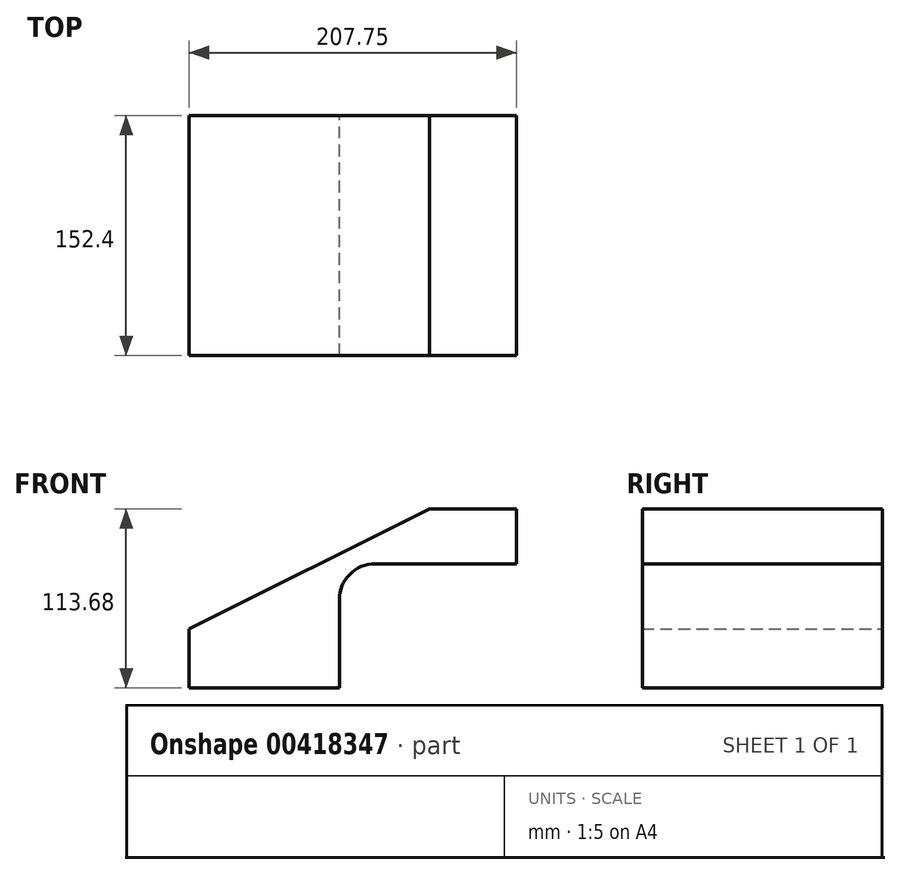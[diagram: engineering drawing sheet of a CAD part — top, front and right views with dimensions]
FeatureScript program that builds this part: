
annotation { "Feature Type Name" : "Feature", "Feature Type Description" : "" }
export const myFeature = defineFeature(function(context is Context, id is Id, definition is map)
    precondition{}
    {
        {
            var Q0;
            Q0=qCreatedBy(makeId("Front.planeOp"),FACE);
            var sketch = newSketch(context, id + "F0", { "sketchPlane" : qUnion([Q0])});
            skLineSegment(sketch, "E0.bottom", {"start": v(47.7, 18.72) * mm, "end": v(-47.7, 18.72) * mm});
            skLineSegment(sketch, "E0.top", {"start": v(47.7, -18.72) * mm, "end": v(-47.7, -18.72) * mm});
            skLineSegment(sketch, "E0.left", {"start": v(47.7, 18.72) * mm, "end": v(47.7, -18.72) * mm});
            skLineSegment(sketch, "E0.right", {"start": v(-47.7, 18.72) * mm, "end": v(-47.7, -18.72) * mm});
            skPoint(sketch, "E0.middle", {"position": v(0, 0) * mm});
            skLineSegment(sketch, "E1", {"start": v(47.7, 18.72) * mm, "end": v(47.7, 37.46) * mm});
            skLineSegment(sketch, "E2.bottom", {"start": v(104.77, 60.19) * mm, "end": v(160.05, 60.19) * mm});
            skLineSegment(sketch, "E2.top", {"start": v(104.77, 94.96) * mm, "end": v(160.05, 94.96) * mm});
            skLineSegment(sketch, "E2.left", {"start": v(104.77, 60.19) * mm, "end": v(104.77, 94.96) * mm});
            skLineSegment(sketch, "E2.right", {"start": v(160.05, 60.19) * mm, "end": v(160.05, 94.96) * mm});
            skPoint(sketch, "E2.middle", {"position": v(132.4, 77.57) * mm});
            skArc(sketch, "E3", {"start": v(47.7, 37.46) * mm, "mid": v(54.36, 53.53) * mm, "end": v(70.43, 60.19) * mm});
            skLineSegment(sketch, "E4", {"start": v(70.43, 60.19) * mm, "end": v(115.47, 60.19) * mm});
            skFitSpline(sketch, "E5", {"points": [v(-47.7, 18.72) * mm, v(104.77, 94.96) * mm], "startDerivative": vector(152.47, 76.24) * mm, "endDerivative": vector(152.47, 76.24) * mm});
            skSolve(sketch);
        }
        {
            var Q0;
            Q0=qCreatedBy(makeId("Front.planeOp"),FACE);
            var sketch = newSketch(context, id + "F1", { "sketchPlane" : qUnion([Q0])});
            skSolve(sketch);
        }
        {
            var Q0;
            Q0 = qSketchRegion(id + "F1", true);
            var Q1;
            Q1=makeQuery(id+"F0.imprint","IMPRINT",FACE,{"disambiguationData":[TD([[makeQuery(id+"F0.imprint","IMPRINT",EDGE,{"derivedFrom":sQuery(id+"F0.wireOp",EDGE,"E0.bottom")}),1.0]])]});
            var Q2;
            {var subQ1=sQuery(id+"F0.wireOp",EDGE,"E2.bottom");Q2=makeQuery(id+"F0.imprint","IMPRINT",FACE,{"disambiguationData":[TD([[makeQuery(id+"F0.imprint","IMPRINT",EDGE,{"derivedFrom":subQ1}),1.0]])]});}
            var Q3;
            Q3=makeQuery(id+"F0.imprint","IMPRINT",FACE,{"disambiguationData":[TD([[makeQuery(id+"F0.imprint","IMPRINT",EDGE,{"derivedFrom":sQuery(id+"F0.wireOp",EDGE,"E0.bottom")}),-1.0]])]});
            extrude(context, id + "F2", {"entities" : qUnion([Q0, Q1, Q2, Q3]), "endBound" : BoundingType.SYMMETRIC, "depth" : 152.4 * mm});
        }
    });
